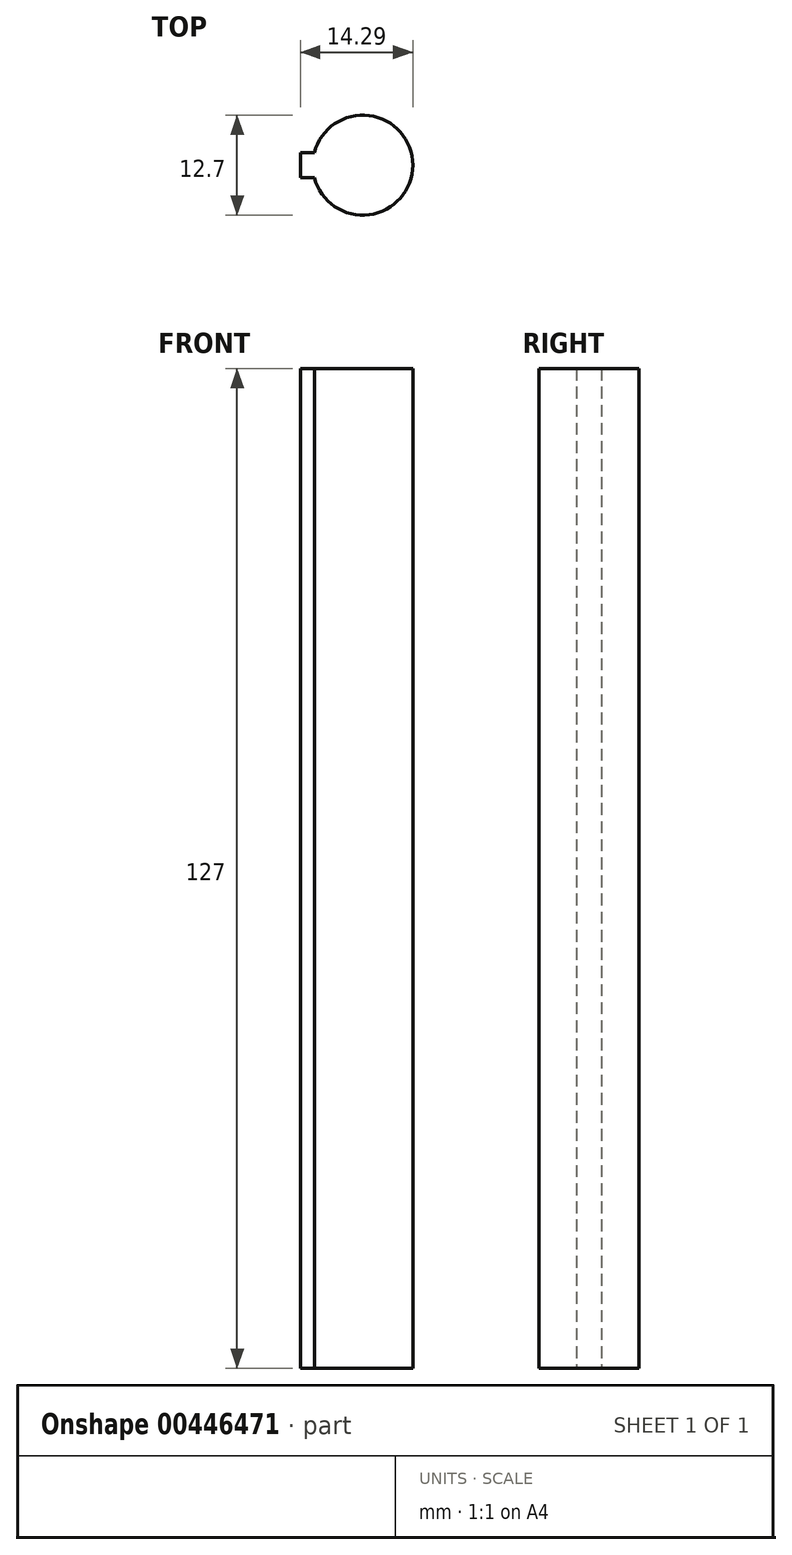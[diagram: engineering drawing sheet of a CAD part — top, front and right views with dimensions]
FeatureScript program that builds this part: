
annotation { "Feature Type Name" : "Feature", "Feature Type Description" : "" }
export const myFeature = defineFeature(function(context is Context, id is Id, definition is map)
    precondition{}
    {
        {
            var Q0;
            Q0=qCreatedBy(makeId("Top.planeOp"),FACE);
            var sketch = newSketch(context, id + "F0", { "sketchPlane" : qUnion([Q0])});
            skArc(sketch, "E0", {"start": v(-6.15, -1.59) * mm, "mid": v(6.35, 0) * mm, "end": v(-6.15, 1.59) * mm});
            skLineSegment(sketch, "E1.bottom", {"start": v(-6.15, -1.59) * mm, "end": v(-7.94, -1.59) * mm});
            skLineSegment(sketch, "E1.top", {"start": v(-6.15, 1.59) * mm, "end": v(-7.94, 1.59) * mm});
            skLineSegment(sketch, "E1.right", {"start": v(-7.94, -1.59) * mm, "end": v(-7.94, 1.59) * mm});
            skSolve(sketch);
        }
        {
            var Q0;
            Q0=makeQuery(id+"F0.imprint","IMPRINT",FACE,{"disambiguationData":[TD([[makeQuery(id+"F0.imprint","IMPRINT",EDGE,{"derivedFrom":sQuery(id+"F0.wireOp",EDGE,"E0")}),1.0]])]});
            extrude(context, id + "F1", {"entities" : qUnion([Q0]), "depth" : 127 * mm, "offsetDistance" : 25.4 * mm, "symmetric" : true});
        }
    });
